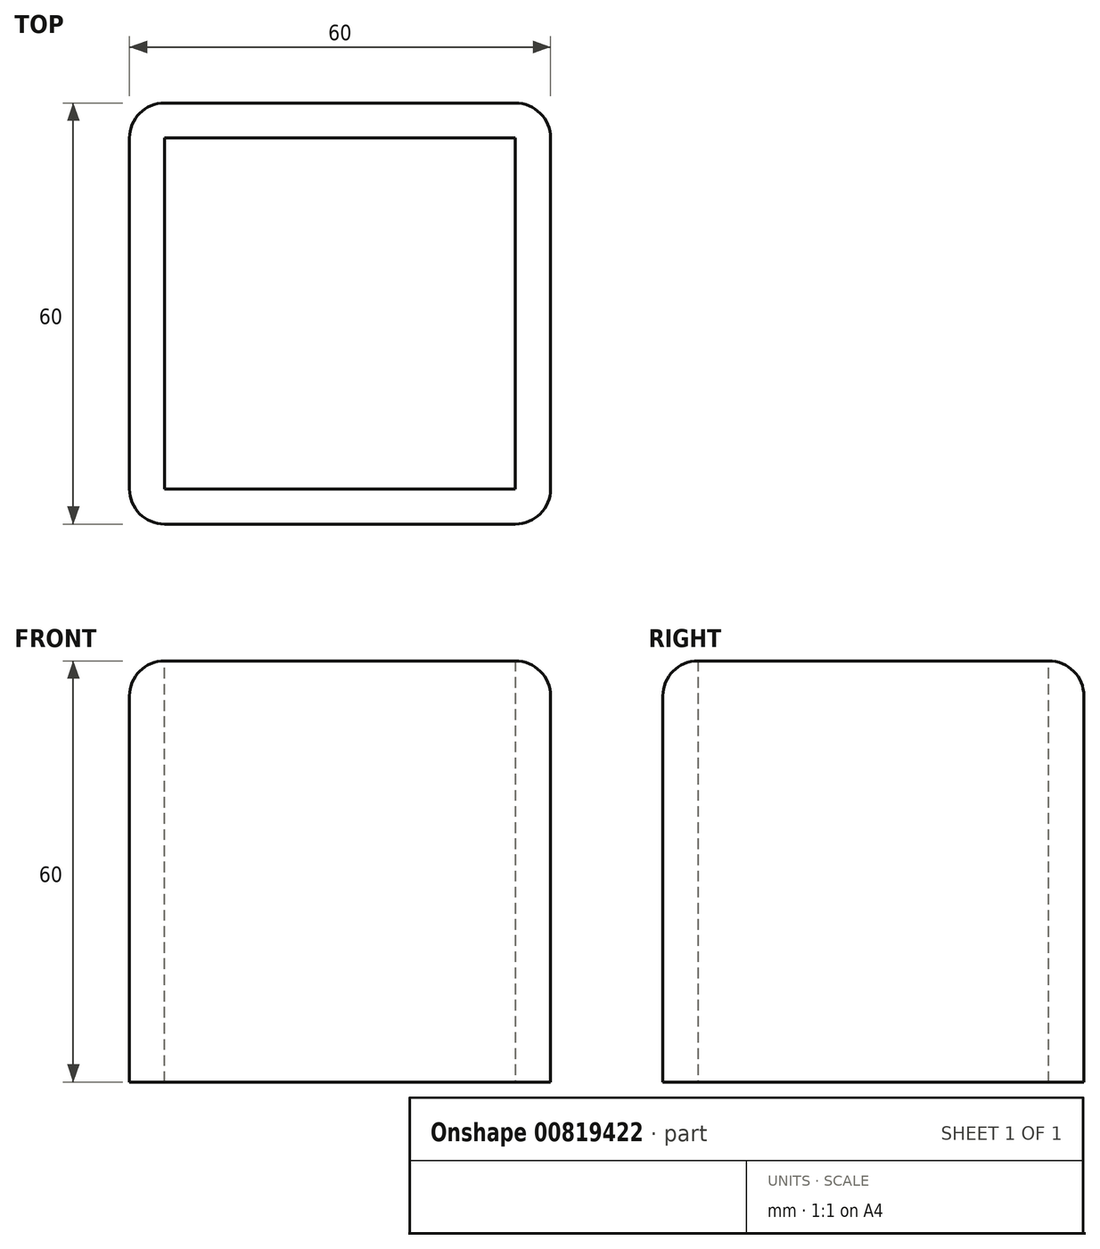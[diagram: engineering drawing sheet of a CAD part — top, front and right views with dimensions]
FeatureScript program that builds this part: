
annotation { "Feature Type Name" : "Feature", "Feature Type Description" : "" }
export const myFeature = defineFeature(function(context is Context, id is Id, definition is map)
    precondition{}
    {
        {
            var Q0;
            Q0=qCreatedBy(makeId("Top.planeOp"),FACE);
            var sketch = newSketch(context, id + "F0", { "sketchPlane" : qUnion([Q0])});
            skLineSegment(sketch, "E0.bottom", {"start": v(-12.55, -31.67) * mm, "end": v(47.45, -31.67) * mm});
            skLineSegment(sketch, "E0.top", {"start": v(-12.55, 28.33) * mm, "end": v(47.45, 28.33) * mm});
            skLineSegment(sketch, "E0.left", {"start": v(-12.55, -31.67) * mm, "end": v(-12.55, 28.33) * mm});
            skLineSegment(sketch, "E0.right", {"start": v(47.45, -31.67) * mm, "end": v(47.45, 28.33) * mm});
            skSolve(sketch);
        }
        {
            var Q0;
            Q0=makeQuery(id+"F0.imprint","IMPRINT",FACE,{"disambiguationData":[TD([[makeQuery(id+"F0.imprint","IMPRINT",EDGE,{"derivedFrom":sQuery(id+"F0.wireOp",EDGE,"E0.bottom")}),1.0]])]});
            extrude(context, id + "F1", {"entities" : qUnion([Q0]), "depth" : 60 * mm});
        }
        {
            var Q0;
            Q0=makeQuery(id+"F1.opExtrude","CAP_EDGE",EDGE,{"disambiguationData":[OSD([sQuery(id+"F0.wireOp",EDGE,"E0.bottom")])],"isStart":false});
            var Q1;
            Q1=makeQuery(id+"F1.opExtrude","CAP_EDGE",EDGE,{"disambiguationData":[OSD([sQuery(id+"F0.wireOp",EDGE,"E0.right")])],"isStart":false});
            var Q2;
            Q2=makeQuery(id+"F1.opExtrude","CAP_EDGE",EDGE,{"disambiguationData":[OSD([sQuery(id+"F0.wireOp",EDGE,"E0.left")])],"isStart":false});
            var Q3;
            Q3=makeQuery(id+"F1.opExtrude","CAP_EDGE",EDGE,{"disambiguationData":[OSD([sQuery(id+"F0.wireOp",EDGE,"E0.top")])],"isStart":false});
            var Q4;
            Q4=makeQuery(id+"F1.opExtrude","SWEPT_EDGE",EDGE,{"disambiguationData":[OSD([sQuery(id+"F0.wireOp",EDGE,"E0.top"),sQuery(id+"F0.wireOp",EDGE,"E0.right")])]});
            var Q5;
            Q5=makeQuery(id+"F1.opExtrude","SWEPT_EDGE",EDGE,{"disambiguationData":[OSD([sQuery(id+"F0.wireOp",EDGE,"E0.bottom"),sQuery(id+"F0.wireOp",EDGE,"E0.right")])]});
            var Q6;
            Q6=makeQuery(id+"F1.opExtrude","SWEPT_EDGE",EDGE,{"disambiguationData":[OSD([sQuery(id+"F0.wireOp",EDGE,"E0.top"),sQuery(id+"F0.wireOp",EDGE,"E0.left")])]});
            fillet(context, id + "F2", {"entities" : qUnion([Q0, Q1, Q2, Q3, Q4, Q5, Q6]), "radius" : 5 * mm, "tangentPropagation" : true, "allowEdgeOverflow" : false});
        }
        {
            var Q0;
            Q0=makeQuery(id+"F1.opExtrude","SWEPT_EDGE",EDGE,{"disambiguationData":[OSD([sQuery(id+"F0.wireOp",EDGE,"E0.bottom"),sQuery(id+"F0.wireOp",EDGE,"E0.left")])]});
            fillet(context, id + "F3", {"entities" : qUnion([Q0]), "radius" : 5 * mm, "tangentPropagation" : true, "allowEdgeOverflow" : false});
        }
        {
            var Q0;
            Q0=makeQuery(id+"F1.opExtrude","CAP_FACE",FACE,{"disambiguationData":[OSD([sQuery(id+"F0.wireOp",EDGE,"E0.bottom"),sQuery(id+"F0.wireOp",EDGE,"E0.top"),sQuery(id+"F0.wireOp",EDGE,"E0.left"),sQuery(id+"F0.wireOp",EDGE,"E0.right")])],"isStart":true});
            shell(context, id + "F4", {"entities" : qUnion([Q0]), "thickness" : 5 * mm});
        }
        {
            var Q0;
            Q0=makeQuery(id+"F1.opExtrude","CAP_FACE",FACE,{"disambiguationData":[OSD([sQuery(id+"F0.wireOp",EDGE,"E0.bottom"),sQuery(id+"F0.wireOp",EDGE,"E0.top"),sQuery(id+"F0.wireOp",EDGE,"E0.left"),sQuery(id+"F0.wireOp",EDGE,"E0.right")])],"isStart":false});
            extrude(context, id + "F5", {"entities" : qUnion([Q0]), "operationType" : NewBodyOperationType.REMOVE, "endBound" : BoundingType.SYMMETRIC, "depth" : 25 * mm, "offsetDistance" : 25 * mm});
        }
    });
